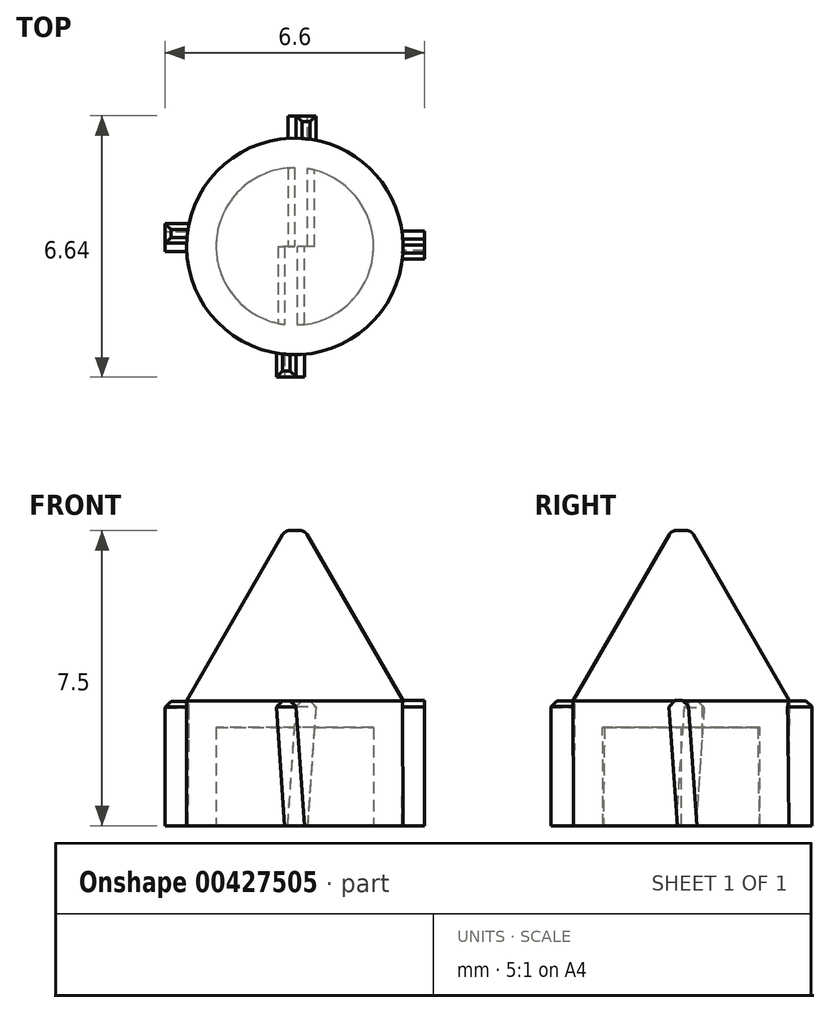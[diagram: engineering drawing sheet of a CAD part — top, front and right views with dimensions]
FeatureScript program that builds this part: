
annotation { "Feature Type Name" : "Feature", "Feature Type Description" : "" }
export const myFeature = defineFeature(function(context is Context, id is Id, definition is map)
    precondition{}
    {
        {
            var Q0;
            Q0=qCreatedBy(makeId("Top.planeOp"),FACE);
            var sketch = newSketch(context, id + "F0", { "sketchPlane" : qUnion([Q0])});
            skCircle(sketch, "E0", {"center": v(0, 0) * mm, "radius": 2.75 * mm});
            skSolve(sketch);
        }
        {
            var Q0;
            Q0 = qSketchRegion(id + "F0", true);
            extrude(context, id + "F1", {"entities" : qUnion([Q0]), "depth" : 9 * mm});
        }
        {
            var Q0;
            Q0=makeQuery(id+"F1.opExtrude","CAP_EDGE",EDGE,{"disambiguationData":[OSD([sQuery(id+"F0.wireOp",EDGE,"E0")])],"isStart":false});
            chamfer(context, id + "F2", {"entities" : qUnion([Q0]), "chamferType" : ChamferType.OFFSET_ANGLE, "width" : 2.5 * mm, "oppositeDirection" : false, "angle" : 60 * degree, "tangentPropagation" : true});
        }
        {
            var Q0;
            {var subQ0=sQuery(id+"F0.wireOp",EDGE,"E0");Q0=makeQuery(id+"F2.opChamfer","BLEND_EDGE",EDGE,{"blendedFrom":[makeQuery(id+"F1.opExtrude","CAP_EDGE",EDGE,{"disambiguationData":[OSD([subQ0])],"isStart":false}),makeQuery(id+"F1.opExtrude","CAP_FACE",FACE,{"disambiguationData":[OSD([subQ0])],"isStart":false})],"blendedInto":[makeQuery(id+"F1.opExtrude","CAP_FACE",FACE,{"disambiguationData":[OSD([subQ0])],"isStart":false})]});}
            fillet(context, id + "F3", {"entities" : qUnion([Q0]), "radius" : 0.2 * mm, "tangentPropagation" : true, "allowEdgeOverflow" : false});
        }
        {
            var Q0;
            Q0=makeQuery(id+"F1.opExtrude","CAP_FACE",FACE,{"disambiguationData":[OSD([sQuery(id+"F0.wireOp",EDGE,"E0")])],"isStart":true});
            var sketch = newSketch(context, id + "F4", { "sketchPlane" : qUnion([Q0])});
            skCircle(sketch, "E1", {"center": v(0, 0) * mm, "radius": 2 * mm});
            skSolve(sketch);
        }
        {
            var Q0;
            Q0 = qSketchRegion(id + "F4", true);
            extrude(context, id + "F5", {"entities" : qUnion([Q0]), "operationType" : NewBodyOperationType.REMOVE, "oppositeDirection" : true, "depth" : 4 * mm});
        }
        {
            var Q0;
            Q0=qCreatedBy(makeId("Right.planeOp"),FACE);
            cPlane(context, id + "F6", {"entities" : qUnion([Q0]), "cplaneType" : CPlaneType.OFFSET, "offset" : 2.3 * mm, "width" : 150 * mm, "height" : 150 * mm});
        }
        {
            var Q0;
            Q0=qCreatedBy(id+"F6.planeOp",FACE);
            var sketch = newSketch(context, id + "F7", { "sketchPlane" : qUnion([Q0])});
            skLineSegment(sketch, "E2", {"start": v(0, 0) * mm, "end": v(-0.33, 4.68) * mm});
            skLineSegment(sketch, "E3", {"start": v(0.5, 0) * mm, "end": v(0.17, 4.68) * mm});
            skLineSegment(sketch, "E4", {"start": v(0.17, 4.68) * mm, "end": v(-0.33, 4.68) * mm});
            skLineSegment(sketch, "E5", {"start": v(0, 0) * mm, "end": v(0.5, 0) * mm});
            skSolve(sketch);
        }
        {
            var Q0;
            Q0 = qSketchRegion(id + "F7", true);
            extrude(context, id + "F8", {"entities" : qUnion([Q0]), "operationType" : NewBodyOperationType.ADD, "depth" : 1 * mm});
        }
        {
            var Q0;
            Q0=makeQuery(id+"F8.opExtrude","SWEPT_EDGE",EDGE,{"disambiguationData":[OSD([sQuery(id+"F7.wireOp",EDGE,"E3"),sQuery(id+"F7.wireOp",EDGE,"E4")])]});
            var Q1;
            Q1=makeQuery(id+"F8.opExtrude","CAP_EDGE",EDGE,{"disambiguationData":[OSD([sQuery(id+"F7.wireOp",EDGE,"E4")])],"isStart":false});
            var Q2;
            Q2=makeQuery(id+"F8.opExtrude","SWEPT_EDGE",EDGE,{"disambiguationData":[OSD([sQuery(id+"F7.wireOp",EDGE,"E2"),sQuery(id+"F7.wireOp",EDGE,"E4")])]});
            chamfer(context, id + "F9", {"entities" : qUnion([Q0, Q1, Q2]), "width" : 0.15 * mm, "tangentPropagation" : true});
        }
        {
            var Q0;
            Q0=qCreatedBy(id+"F6.planeOp",FACE);
            cPlane(context, id + "F10", {"entities" : qUnion([Q0]), "cplaneType" : CPlaneType.OFFSET, "offset" : 5 * mm, "oppositeDirection" : true, "width" : 150 * mm, "height" : 150 * mm});
        }
        {
            var Q0;
            Q0=qCreatedBy(id+"F10.planeOp",FACE);
            var sketch = newSketch(context, id + "F11", { "sketchPlane" : qUnion([Q0])});
            skLineSegment(sketch, "E6", {"start": v(-0.23, 0) * mm, "end": v(0.1, 4.66) * mm});
            skLineSegment(sketch, "E7", {"start": v(0.1, 4.66) * mm, "end": v(0.6, 4.66) * mm});
            skLineSegment(sketch, "E8", {"start": v(0.6, 4.66) * mm, "end": v(0.27, 0) * mm});
            skLineSegment(sketch, "E9", {"start": v(0.27, 0) * mm, "end": v(-0.23, 0) * mm});
            skSolve(sketch);
        }
        {
            var Q0;
            Q0 = qSketchRegion(id + "F11", true);
            extrude(context, id + "F12", {"entities" : qUnion([Q0]), "operationType" : NewBodyOperationType.ADD, "oppositeDirection" : true, "depth" : 0.6 * mm});
        }
        {
            var Q0;
            Q0=makeQuery(id+"F12.opExtrude","SWEPT_EDGE",EDGE,{"disambiguationData":[OSD([sQuery(id+"F11.wireOp",EDGE,"E6"),sQuery(id+"F11.wireOp",EDGE,"E7")])]});
            var Q1;
            Q1=makeQuery(id+"F12.opExtrude","SWEPT_EDGE",EDGE,{"disambiguationData":[OSD([sQuery(id+"F11.wireOp",EDGE,"E7"),sQuery(id+"F11.wireOp",EDGE,"E8")])]});
            var Q2;
            Q2=makeQuery(id+"F12.opExtrude","CAP_EDGE",EDGE,{"disambiguationData":[OSD([sQuery(id+"F11.wireOp",EDGE,"E7")])],"isStart":false});
            chamfer(context, id + "F13", {"entities" : qUnion([Q0, Q1, Q2]), "width" : 0.15 * mm, "tangentPropagation" : true});
        }
        {
            var Q0;
            Q0=qCreatedBy(makeId("Front.planeOp"),FACE);
            var sketch = newSketch(context, id + "F14", { "sketchPlane" : qUnion([Q0])});
            skLineSegment(sketch, "E10", {"start": v(-0.28, 0) * mm, "end": v(0.04, 4.68) * mm});
            skLineSegment(sketch, "E11", {"start": v(0.04, 4.68) * mm, "end": v(0.54, 4.68) * mm});
            skLineSegment(sketch, "E12", {"start": v(0.54, 4.68) * mm, "end": v(0.22, 0) * mm});
            skLineSegment(sketch, "E13", {"start": v(0.22, 0) * mm, "end": v(-0.28, 0) * mm});
            skSolve(sketch);
        }
        {
            var Q0;
            Q0 = qSketchRegion(id + "F14", true);
            extrude(context, id + "F15", {"entities" : qUnion([Q0]), "operationType" : NewBodyOperationType.ADD, "oppositeDirection" : true, "depth" : 3.32 * mm});
        }
        {
            var Q0;
            Q0=makeQuery(id+"F15.opExtrude","CAP_EDGE",EDGE,{"disambiguationData":[OSD([sQuery(id+"F14.wireOp",EDGE,"E11")])],"isStart":false});
            var Q1;
            Q1=makeQuery(id+"F15.opExtrude","SWEPT_EDGE",EDGE,{"disambiguationData":[OSD([sQuery(id+"F14.wireOp",EDGE,"E10"),sQuery(id+"F14.wireOp",EDGE,"E11")])]});
            var Q2;
            Q2=makeQuery(id+"F15.opExtrude","SWEPT_EDGE",EDGE,{"disambiguationData":[OSD([sQuery(id+"F14.wireOp",EDGE,"E11"),sQuery(id+"F14.wireOp",EDGE,"E12")])]});
            chamfer(context, id + "F16", {"entities" : qUnion([Q0, Q1, Q2]), "width" : 0.15 * mm, "tangentPropagation" : true});
        }
        {
            var Q0;
            Q0=qCreatedBy(makeId("Front.planeOp"),FACE);
            var sketch = newSketch(context, id + "F17", { "sketchPlane" : qUnion([Q0])});
            skLineSegment(sketch, "E14", {"start": v(0.35, 0) * mm, "end": v(0.02, 4.67) * mm});
            skLineSegment(sketch, "E15", {"start": v(0.02, 4.67) * mm, "end": v(-0.48, 4.67) * mm});
            skLineSegment(sketch, "E16", {"start": v(-0.48, 4.67) * mm, "end": v(-0.15, 0) * mm});
            skLineSegment(sketch, "E17", {"start": v(-0.15, 0) * mm, "end": v(0.35, 0) * mm});
            skSolve(sketch);
        }
        {
            var Q0;
            Q0 = qSketchRegion(id + "F17", true);
            extrude(context, id + "F18", {"entities" : qUnion([Q0]), "operationType" : NewBodyOperationType.ADD, "depth" : 3.32 * mm});
        }
        {
            var Q0;
            Q0=makeQuery(id+"F18.opExtrude","SWEPT_EDGE",EDGE,{"disambiguationData":[OSD([sQuery(id+"F17.wireOp",EDGE,"E15"),sQuery(id+"F17.wireOp",EDGE,"E16")])]});
            var Q1;
            Q1=makeQuery(id+"F18.opExtrude","SWEPT_EDGE",EDGE,{"disambiguationData":[OSD([sQuery(id+"F17.wireOp",EDGE,"E14"),sQuery(id+"F17.wireOp",EDGE,"E15")])]});
            var Q2;
            Q2=makeQuery(id+"F18.opExtrude","CAP_EDGE",EDGE,{"disambiguationData":[OSD([sQuery(id+"F17.wireOp",EDGE,"E15")])],"isStart":false});
            chamfer(context, id + "F19", {"entities" : qUnion([Q0, Q1, Q2]), "width" : 0.15 * mm, "tangentPropagation" : true});
        }
        {
            var Q0;
            Q0=qCreatedBy(makeId("Top.planeOp"),FACE);
            var sketch = newSketch(context, id + "F20", { "sketchPlane" : qUnion([Q0])});
            skCircle(sketch, "E18", {"center": v(0, 0) * mm, "radius": 3.92 * mm});
            skSolve(sketch);
        }
        {
            var Q0;
            Q0 = qSketchRegion(id + "F20", true);
            extrude(context, id + "F21", {"entities" : qUnion([Q0]), "operationType" : NewBodyOperationType.REMOVE, "depth" : 1.5 * mm});
        }
    });
